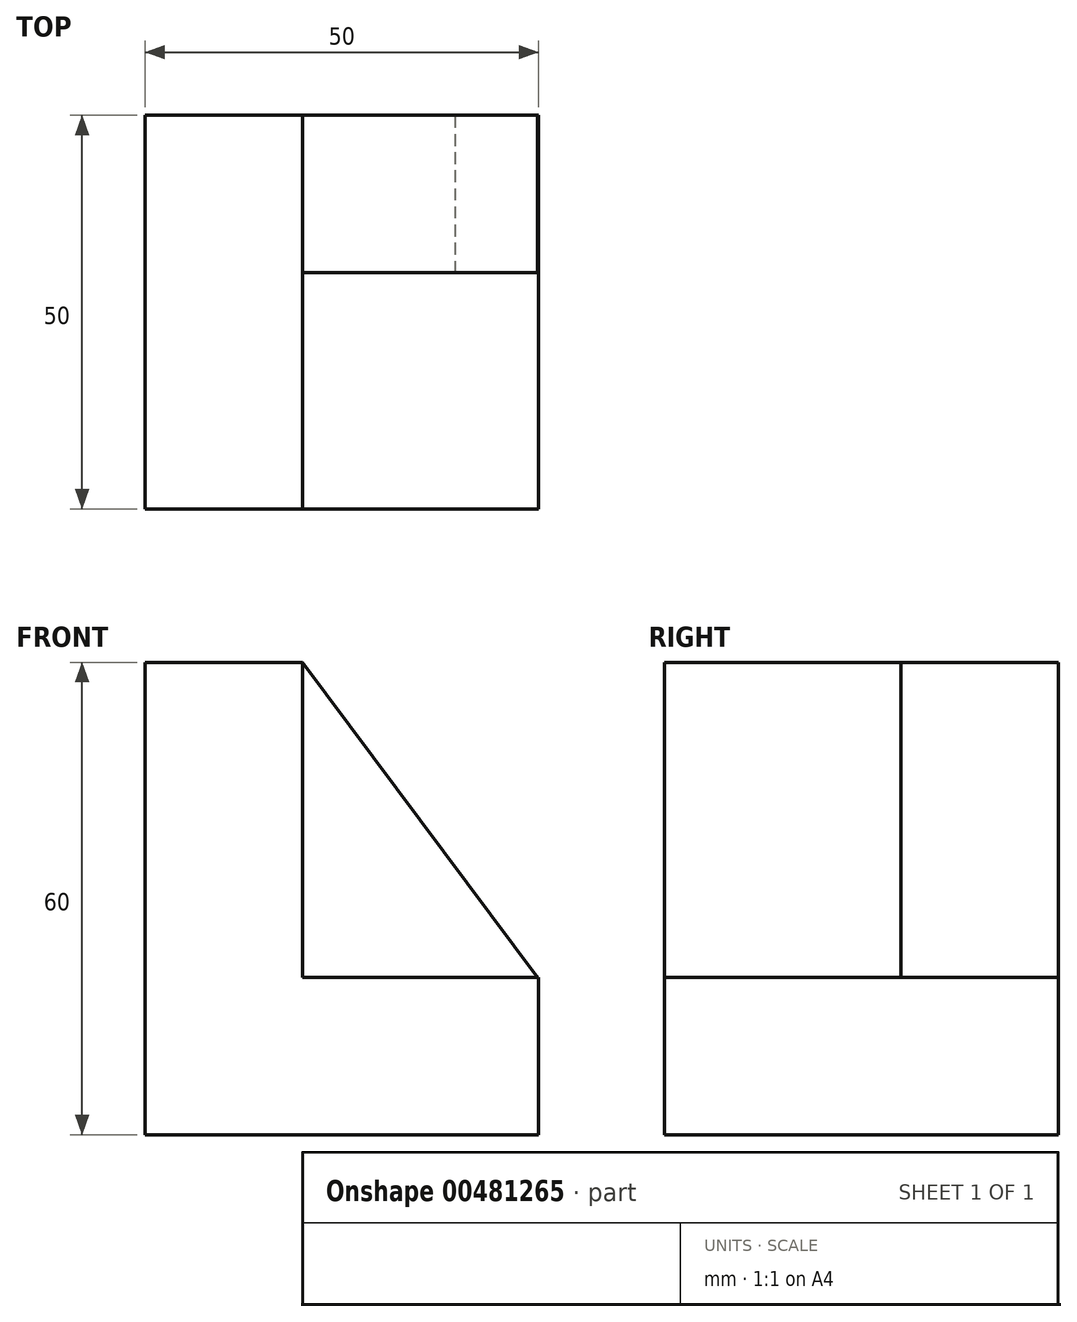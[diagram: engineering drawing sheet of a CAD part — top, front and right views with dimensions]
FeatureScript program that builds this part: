
annotation { "Feature Type Name" : "Feature", "Feature Type Description" : "" }
export const myFeature = defineFeature(function(context is Context, id is Id, definition is map)
    precondition{}
    {
        {
            var Q0;
            Q0=qCreatedBy(makeId("Front.planeOp"),FACE);
            var sketch = newSketch(context, id + "F0", { "sketchPlane" : qUnion([Q0])});
            skLineSegment(sketch, "E0", {"start": v(0, 0) * mm, "end": v(0, 60) * mm});
            skLineSegment(sketch, "E1", {"start": v(0, 60) * mm, "end": v(20, 60) * mm});
            skLineSegment(sketch, "E2", {"start": v(20, 60) * mm, "end": v(20, 20) * mm});
            skLineSegment(sketch, "E3", {"start": v(20, 20) * mm, "end": v(50, 20) * mm});
            skLineSegment(sketch, "E4", {"start": v(50, 20) * mm, "end": v(50, 0) * mm});
            skLineSegment(sketch, "E5", {"start": v(50, 0) * mm, "end": v(0, 0) * mm});
            skSolve(sketch);
        }
        {
            var Q0;
            Q0=makeQuery(id+"F0.imprint","IMPRINT",FACE,{"disambiguationData":[TD([[makeQuery(id+"F0.imprint","IMPRINT",EDGE,{"derivedFrom":sQuery(id+"F0.wireOp",EDGE,"E0")}),-1.0]])]});
            extrude(context, id + "F1", {"entities" : qUnion([Q0]), "depth" : 50 * mm});
        }
        {
            var Q0;
            Q0=makeQuery(id+"F0.imprint","IMPRINT",FACE,{"disambiguationData":[TD([[makeQuery(id+"F0.imprint","IMPRINT",EDGE,{"derivedFrom":sQuery(id+"F0.wireOp",EDGE,"E0")}),-1.0]])]});
            var sketch = newSketch(context, id + "F2", { "sketchPlane" : qUnion([Q0])});
            skLineSegment(sketch, "E6", {"start": v(49.88, 19.96) * mm, "end": v(19.98, 60) * mm});
            skLineSegment(sketch, "E7", {"start": v(19.98, 60) * mm, "end": v(19.98, 20.07) * mm});
            skLineSegment(sketch, "E8", {"start": v(19.98, 20.07) * mm, "end": v(49.88, 19.96) * mm});
            skSolve(sketch);
        }
        {
            var Q0;
            {var subQ0=sQuery(id+"F2.wireOp",EDGE,"E6");var subQ1=makeQuery(id+"F0.imprint","IMPRINT",EDGE,{"derivedFrom":sQuery(id+"F0.wireOp",EDGE,"E3")});var subQ2=makeQuery(id+"F2.imprint","INTERSECT",VERTEX,{"derivedFrom":[subQ1,subQ0]});Q0=makeQuery(id+"F2.imprint","IMPRINT",FACE,{"disambiguationData":[TD([[makeQuery(id+"F2.imprint","IMPRINT",EDGE,{"disambiguationData":[TD([[subQ2,-1.0]])],"derivedFrom":subQ0}),1.0]])]});}
            extrude(context, id + "F3", {"entities" : qUnion([Q0]), "operationType" : NewBodyOperationType.ADD, "depth" : 20 * mm});
        }
    });
